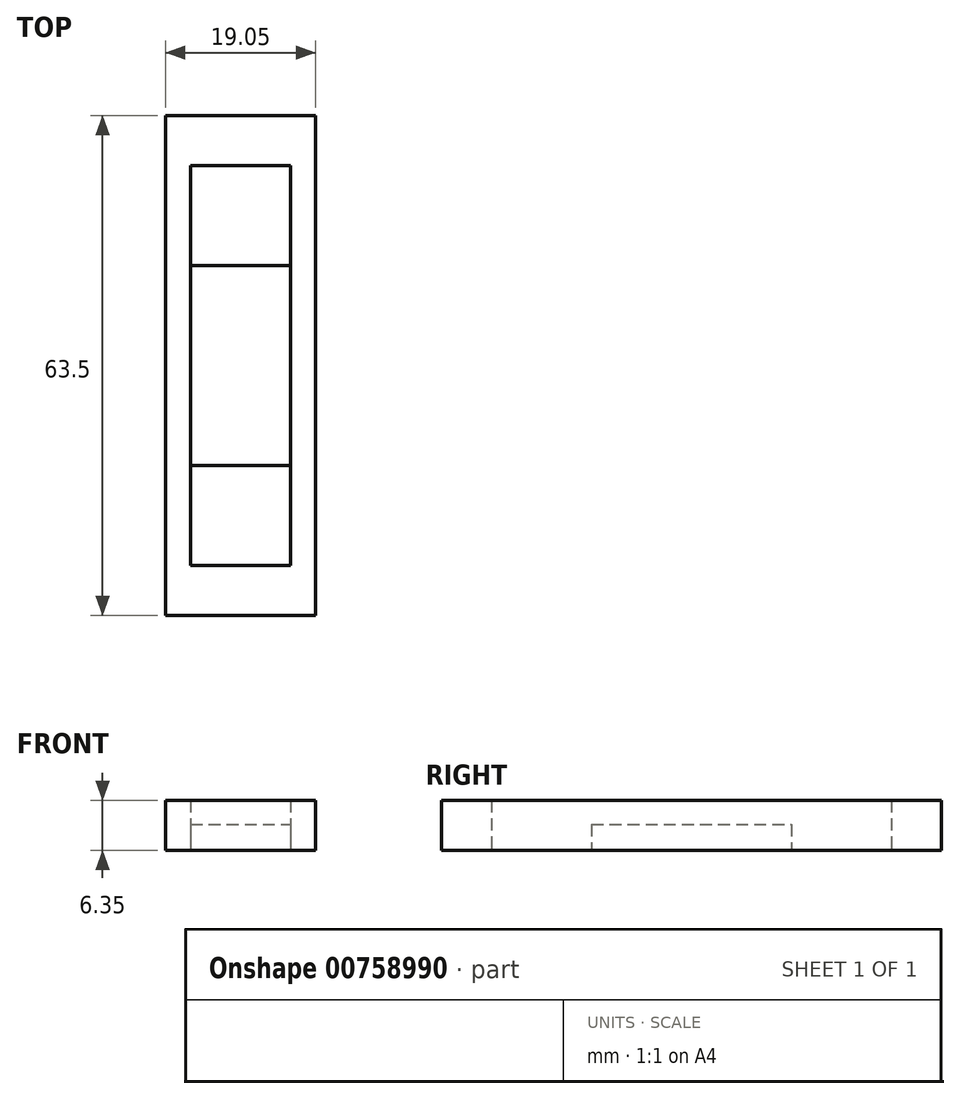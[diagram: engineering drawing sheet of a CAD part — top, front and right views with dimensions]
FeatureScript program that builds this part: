
annotation { "Feature Type Name" : "Feature", "Feature Type Description" : "" }
export const myFeature = defineFeature(function(context is Context, id is Id, definition is map)
    precondition{}
    {
        {
            var Q0;
            Q0=qCreatedBy(makeId("Top.planeOp"),FACE);
            var sketch = newSketch(context, id + "F0", { "sketchPlane" : qUnion([Q0])});
            skLineSegment(sketch, "E0.bottom", {"start": v(-39.4, -69.2) * mm, "end": v(-26.7, -69.2) * mm});
            skLineSegment(sketch, "E0.top", {"start": v(-39.4, -18.4) * mm, "end": v(-26.7, -18.4) * mm});
            skLineSegment(sketch, "E0.left", {"start": v(-39.4, -69.2) * mm, "end": v(-39.4, -18.4) * mm});
            skLineSegment(sketch, "E0.right", {"start": v(-26.7, -69.2) * mm, "end": v(-26.7, -18.4) * mm});
            skLineSegment(sketch, "E1.bottom", {"start": v(-42.57, -75.54) * mm, "end": v(-23.52, -75.54) * mm});
            skLineSegment(sketch, "E1.left", {"start": v(-42.57, -75.54) * mm, "end": v(-42.57, -12.04) * mm});
            skLineSegment(sketch, "E1.right", {"start": v(-23.52, -75.54) * mm, "end": v(-23.52, -12.04) * mm});
            skLineSegment(sketch, "E2.bottom", {"start": v(-23.52, -12.04) * mm, "end": v(-42.57, -12.04) * mm});
            skSolve(sketch);
        }
        {
            var Q0;
            Q0=makeQuery(id+"F0.imprint","IMPRINT",FACE,{"disambiguationData":[TD([[makeQuery(id+"F0.imprint","IMPRINT",EDGE,{"derivedFrom":sQuery(id+"F0.wireOp",EDGE,"E0.bottom")}),-1.0]])]});
            extrude(context, id + "F1", {"entities" : qUnion([Q0]), "depth" : 6.35 * mm, "offsetDistance" : 25.4 * mm});
        }
        {
            var Q0;
            Q0=qCreatedBy(makeId("Top.planeOp"),FACE);
            var sketch = newSketch(context, id + "F2", { "sketchPlane" : qUnion([Q0])});
            skLineSegment(sketch, "E3.bottom", {"start": v(-39.4, -56.5) * mm, "end": v(-26.7, -56.5) * mm});
            skLineSegment(sketch, "E3.top", {"start": v(-39.4, -31.1) * mm, "end": v(-26.7, -31.1) * mm});
            skLineSegment(sketch, "E3.left", {"start": v(-39.4, -56.5) * mm, "end": v(-39.4, -31.1) * mm});
            skLineSegment(sketch, "E3.right", {"start": v(-26.7, -56.5) * mm, "end": v(-26.7, -31.1) * mm});
            skSolve(sketch);
        }
        {
            var Q0;
            Q0=makeQuery(id+"F2.imprint","IMPRINT",FACE,{"disambiguationData":[TD([[makeQuery(id+"F2.imprint","IMPRINT",EDGE,{"derivedFrom":sQuery(id+"F2.wireOp",EDGE,"E3.bottom")}),1.0]])]});
            extrude(context, id + "F3", {"entities" : qUnion([Q0]), "operationType" : NewBodyOperationType.ADD, "depth" : 3.3 * mm, "offsetDistance" : 25.4 * mm});
        }
        {
            var Q0;
            Q0=makeQuery(id+"F3.opExtrude","CAP_FACE",FACE,{"disambiguationData":[OSD([sQuery(id+"F2.wireOp",EDGE,"E3.bottom"),sQuery(id+"F2.wireOp",EDGE,"E3.top"),sQuery(id+"F2.wireOp",EDGE,"E3.left"),sQuery(id+"F2.wireOp",EDGE,"E3.right")])],"isStart":false});
            var sketch = newSketch(context, id + "F4", { "sketchPlane" : qUnion([Q0])});
            skCircle(sketch, "E4", {"center": v(-33.05, -43.8) * mm, "radius": 3.92 * mm});
            skSolve(sketch);
        }
        {
            var Q0;
            Q0=sQuery(id+"F4.wireOp",EDGE,"E4");
            extrude(context, id + "F5", {"bodyType" : ToolBodyType.SURFACE, "surfaceEntities" : qUnion([Q0]), "depth" : 12.7 * mm, "offsetDistance" : 25.4 * mm});
        }
    });
